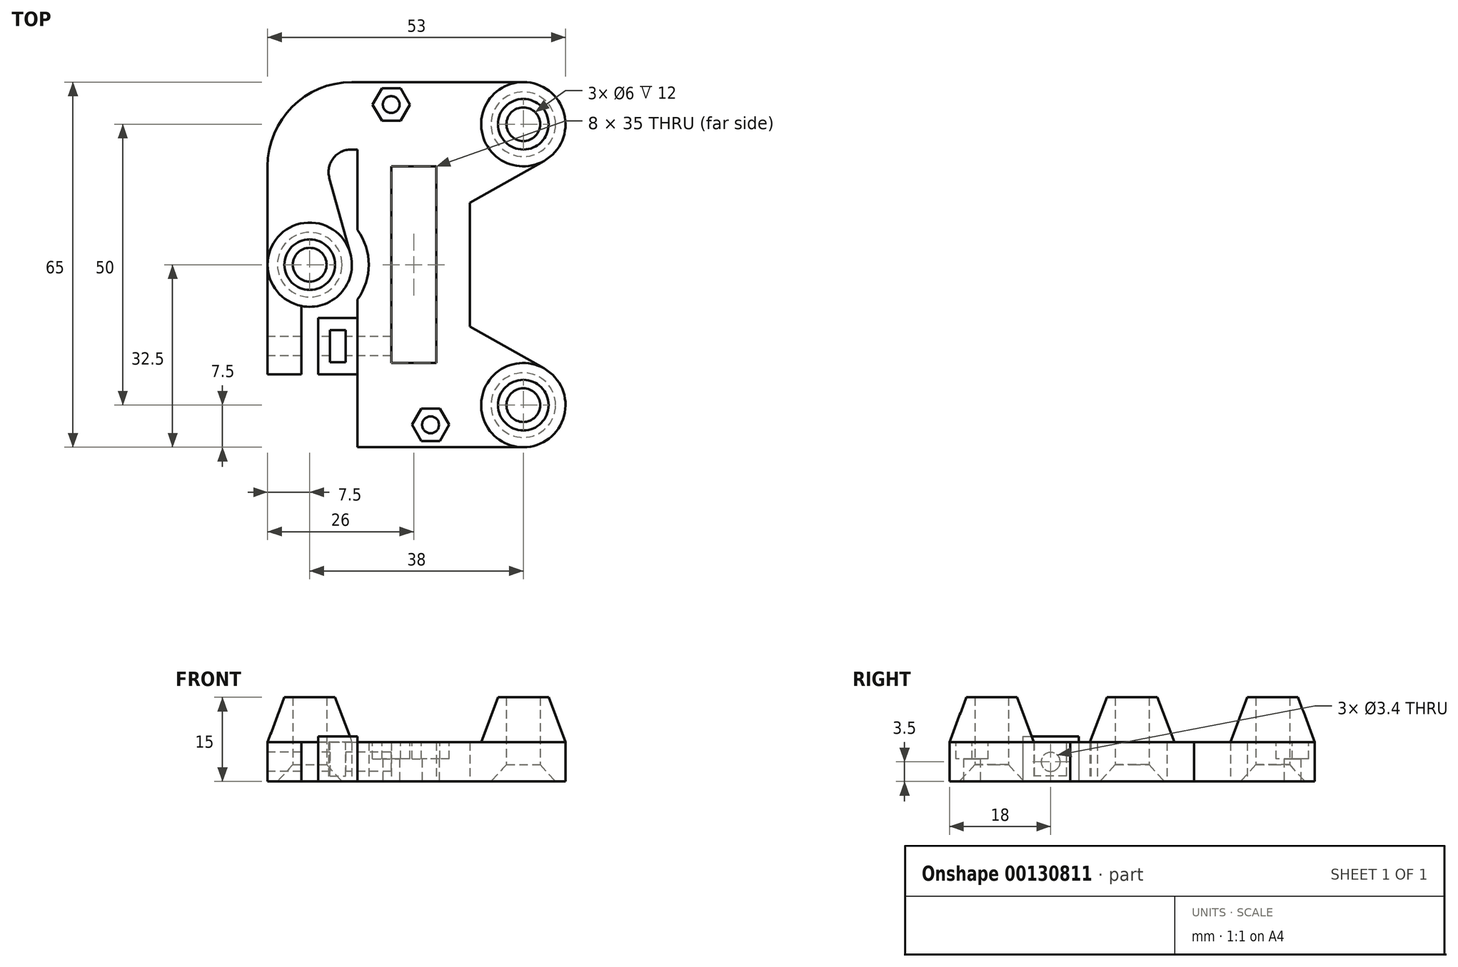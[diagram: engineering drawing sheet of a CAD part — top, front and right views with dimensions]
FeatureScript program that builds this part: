
annotation { "Feature Type Name" : "Feature", "Feature Type Description" : "" }
export const myFeature = defineFeature(function(context is Context, id is Id, definition is map)
    precondition{}
    {
        {
            var Q0;
            Q0=qCreatedBy(makeId("Top.planeOp"),FACE);
            var sketch = newSketch(context, id + "F0", { "sketchPlane" : qUnion([Q0])});
            skLineSegment(sketch, "E0.bottom", {"start": v(0, 0) * mm, "end": v(20, 0) * mm});
            skLineSegment(sketch, "E0.top", {"start": v(0, 65) * mm, "end": v(20, 65) * mm});
            skLineSegment(sketch, "E0.left", {"start": v(0, 0) * mm, "end": v(0, 26.34) * mm});
            skLineSegment(sketch, "E0.right", {"start": v(20, 0) * mm, "end": v(20, 65) * mm});
            skLineSegment(sketch, "E1.bottom", {"start": v(6, 50) * mm, "end": v(14, 50) * mm});
            skLineSegment(sketch, "E1.top", {"start": v(6, 15) * mm, "end": v(14, 15) * mm});
            skLineSegment(sketch, "E1.left", {"start": v(6, 50) * mm, "end": v(6, 15) * mm});
            skLineSegment(sketch, "E1.right", {"start": v(14, 50) * mm, "end": v(14, 15) * mm});
            skLineSegment(sketch, "E2.bottom", {"start": v(-7, 23) * mm, "end": v(0, 23) * mm});
            skLineSegment(sketch, "E2.top", {"start": v(-7, 13) * mm, "end": v(0, 13) * mm});
            skLineSegment(sketch, "E2.left", {"start": v(-7, 23) * mm, "end": v(-7, 13) * mm});
            skLineSegment(sketch, "E2.right", {"start": v(0, 23) * mm, "end": v(0, 13) * mm});
            skCircle(sketch, "E3", {"center": v(29.5, 7.5) * mm, "radius": 3 * mm});
            skCircle(sketch, "E4", {"center": v(29.5, 57.5) * mm, "radius": 3 * mm});
            skCircle(sketch, "E5", {"center": v(-8.5, 32.5) * mm, "radius": 7.5 * mm});
            skCircle(sketch, "E6", {"center": v(29.5, 57.5) * mm, "radius": 7.5 * mm});
            skCircle(sketch, "E7", {"center": v(29.5, 7.5) * mm, "radius": 7.5 * mm});
            skLineSegment(sketch, "E8", {"start": v(20, 0) * mm, "end": v(29.5, 0) * mm});
            skLineSegment(sketch, "E9", {"start": v(20, 65) * mm, "end": v(29.5, 65) * mm});
            skLineSegment(sketch, "E10", {"start": v(-1.27, 34.5) * mm, "end": v(-5, 47.93) * mm});
            skLineSegment(sketch, "E11", {"start": v(-16, 13) * mm, "end": v(-16, 50) * mm});
            skCircle(sketch, "E12", {"center": v(-8.5, 32.5) * mm, "radius": 3 * mm});
            skLineSegment(sketch, "E13", {"start": v(-16, 13) * mm, "end": v(-10, 13) * mm});
            skLineSegment(sketch, "E14", {"start": v(-10, 13) * mm, "end": v(-10, 25.15) * mm});
            skLineSegment(sketch, "E15", {"start": v(-1, 65) * mm, "end": v(0, 65) * mm});
            skCircle(sketch, "E16", {"center": v(6, 61) * mm, "radius": 1.5 * mm});
            skCircle(sketch, "E17", {"center": v(13, 4) * mm, "radius": 1.5 * mm});
            skLineSegment(sketch, "E18", {"start": v(33.2, 50.97) * mm, "end": v(20, 43.5) * mm});
            skLineSegment(sketch, "E19", {"start": v(33.2, 14.03) * mm, "end": v(20, 21.5) * mm});
            skPoint(sketch, "E20.visualSharp", {"position": v(-16, 65) * mm});
            skArc(sketch, "E20.filletArc", {"start": v(-1, 65) * mm, "mid": v(-11.6, 60.6) * mm, "end": v(-16, 50) * mm});
            skLineSegment(sketch, "E21", {"start": v(-1.15, 53) * mm, "end": v(0, 53) * mm});
            skPoint(sketch, "E22", {"position": v(20, 32.5) * mm});
            skArc(sketch, "E23", {"start": v(0, 26.34) * mm, "mid": v(2, 32.5) * mm, "end": v(0, 38.66) * mm});
            skLineSegment(sketch, "E24", {"start": v(6, 32.5) * mm, "end": v(2, 32.5) * mm});
            skLineSegment(sketch, "E25.trimOffspring", {"start": v(0, 38.66) * mm, "end": v(0, 65) * mm});
            skPoint(sketch, "E26.visualSharp", {"position": v(-6.4, 53) * mm});
            skArc(sketch, "E26.filletArc", {"start": v(-1.15, 53) * mm, "mid": v(-4.33, 51.42) * mm, "end": v(-5, 47.93) * mm});
            skPoint(sketch, "E27", {"position": v(37, 57.5) * mm});
            skSolve(sketch);
        }
        {
            var Q0;
            Q0=qSketchRegion(id+"F0",true);
            extrude(context, id + "F1", {"entities" : qUnion([Q0]), "depth" : 7 * mm});
        }
        {
            var Q0;
            Q0=makeQuery(id+"F1.opExtrude","CAP_FACE",FACE,{"disambiguationData":[OSD([sQuery(id+"F0.wireOp",EDGE,"E0.bottom"),sQuery(id+"F0.wireOp",EDGE,"E0.top"),sQuery(id+"F0.wireOp",EDGE,"E0.left"),sQuery(id+"F0.wireOp",EDGE,"E0.right"),sQuery(id+"F0.wireOp",EDGE,"E1.bottom"),sQuery(id+"F0.wireOp",EDGE,"E1.top"),sQuery(id+"F0.wireOp",EDGE,"E1.left"),sQuery(id+"F0.wireOp",EDGE,"E1.right"),sQuery(id+"F0.wireOp",EDGE,"E2.bottom"),sQuery(id+"F0.wireOp",EDGE,"E2.top"),sQuery(id+"F0.wireOp",EDGE,"E2.left"),sQuery(id+"F0.wireOp",EDGE,"E3"),sQuery(id+"F0.wireOp",EDGE,"E4"),sQuery(id+"F0.wireOp",EDGE,"E5"),sQuery(id+"F0.wireOp",EDGE,"E6"),sQuery(id+"F0.wireOp",EDGE,"E7"),sQuery(id+"F0.wireOp",EDGE,"E8"),sQuery(id+"F0.wireOp",EDGE,"E9"),sQuery(id+"F0.wireOp",EDGE,"E10"),sQuery(id+"F0.wireOp",EDGE,"E11"),sQuery(id+"F0.wireOp",EDGE,"E12"),sQuery(id+"F0.wireOp",EDGE,"E13"),sQuery(id+"F0.wireOp",EDGE,"E14"),sQuery(id+"F0.wireOp",EDGE,"E16"),sQuery(id+"F0.wireOp",EDGE,"E17"),sQuery(id+"F0.wireOp",EDGE,"E18"),sQuery(id+"F0.wireOp",EDGE,"E19"),sQuery(id+"F0.wireOp",EDGE,"E20.filletArc"),sQuery(id+"F0.wireOp",EDGE,"E23"),sQuery(id+"F0.wireOp",EDGE,"E25.trimOffspring"),sQuery(id+"F0.wireOp",EDGE,"E26.filletArc")])],"isStart":false});
            cPlane(context, id + "F2", {"entities" : qUnion([Q0]), "cplaneType" : CPlaneType.OFFSET, "offset" : 0 * mm, "width" : 150 * mm, "height" : 150 * mm});
        }
        {
            var Q0;
            Q0=qCreatedBy(id+"F2.planeOp",FACE);
            var sketch = newSketch(context, id + "F3", { "sketchPlane" : qUnion([Q0])});
            skCircle(sketch, "E28.cCircle", {"center": v(13, 4) * mm, "radius": 2.88 * mm, "construction": true});
            skLineSegment(sketch, "E28.0", {"start": v(14.66, 1.13) * mm, "end": v(11.34, 1.12) * mm});
            skLineSegment(sketch, "E28.1", {"start": v(11.34, 1.12) * mm, "end": v(9.68, 4) * mm});
            skLineSegment(sketch, "E28.2", {"start": v(9.68, 4) * mm, "end": v(11.34, 6.88) * mm});
            skLineSegment(sketch, "E28.3", {"start": v(11.34, 6.88) * mm, "end": v(14.66, 6.88) * mm});
            skLineSegment(sketch, "E28.4", {"start": v(14.66, 6.87) * mm, "end": v(16.32, 4) * mm});
            skLineSegment(sketch, "E28.5", {"start": v(16.32, 4) * mm, "end": v(14.66, 1.12) * mm});
            skPoint(sketch, "E28.0.midPoint", {"position": v(13, 1.13) * mm});
            skCircle(sketch, "E29.cCircle", {"center": v(6, 61) * mm, "radius": 2.88 * mm, "construction": true});
            skLineSegment(sketch, "E29.0", {"start": v(9.32, 61) * mm, "end": v(7.66, 58.13) * mm});
            skLineSegment(sketch, "E29.1", {"start": v(7.66, 58.12) * mm, "end": v(4.34, 58.12) * mm});
            skLineSegment(sketch, "E29.2", {"start": v(4.34, 58.12) * mm, "end": v(2.68, 61) * mm});
            skLineSegment(sketch, "E29.3", {"start": v(2.68, 61) * mm, "end": v(4.34, 63.87) * mm});
            skLineSegment(sketch, "E29.4", {"start": v(4.34, 63.88) * mm, "end": v(7.66, 63.88) * mm});
            skLineSegment(sketch, "E29.5", {"start": v(7.66, 63.88) * mm, "end": v(9.32, 61) * mm});
            skPoint(sketch, "E29.0.midPoint", {"position": v(8.49, 59.56) * mm});
            skSolve(sketch);
        }
        {
            var Q0;
            Q0=qSketchRegion(id+"F3",true);
            extrude(context, id + "F4", {"entities" : qUnion([Q0]), "operationType" : NewBodyOperationType.REMOVE, "flatOperationType" : FlatOperationType.REMOVE, "oppositeDirection" : true, "offsetDistance" : 25 * mm, "depth" : 3 * mm, "domain" : OperationDomain.MODEL});
        }
        {
            var Q0;
            Q0=qCreatedBy(id+"F2.planeOp",FACE);
            var sketch = newSketch(context, id + "F5", { "sketchPlane" : qUnion([Q0])});
            skLineSegment(sketch, "E30.bottom", {"start": v(-7, 13) * mm, "end": v(0, 13) * mm});
            skLineSegment(sketch, "E30.top", {"start": v(-7, 23) * mm, "end": v(0, 23) * mm});
            skLineSegment(sketch, "E30.left", {"start": v(-7, 13) * mm, "end": v(-7, 23) * mm});
            skLineSegment(sketch, "E30.right", {"start": v(0, 13) * mm, "end": v(0, 23) * mm});
            skSolve(sketch);
        }
        {
            var Q0;
            Q0=qSketchRegion(id+"F5",true);
            extrude(context, id + "F6", {"entities" : qUnion([Q0]), "operationType" : NewBodyOperationType.ADD, "depth" : 1 * mm});
        }
        {
            var Q0;
            Q0=makeQuery(id+"F6.opExtrude","CAP_FACE",FACE,{"disambiguationData":[OSD([sQuery(id+"F5.wireOp",EDGE,"E30.bottom"),sQuery(id+"F5.wireOp",EDGE,"E30.top"),sQuery(id+"F5.wireOp",EDGE,"E30.left"),sQuery(id+"F5.wireOp",EDGE,"E30.right")])],"isStart":false});
            cPlane(context, id + "F7", {"entities" : qUnion([Q0]), "cplaneType" : CPlaneType.OFFSET, "offset" : 0 * mm, "width" : 150 * mm, "height" : 150 * mm});
        }
        {
            var Q0;
            Q0=qCreatedBy(id+"F7.planeOp",FACE);
            var sketch = newSketch(context, id + "F8", { "sketchPlane" : qUnion([Q0])});
            skLineSegment(sketch, "E31.bottom", {"start": v(-4.87, 20.88) * mm, "end": v(-2.12, 20.88) * mm});
            skLineSegment(sketch, "E31.top", {"start": v(-4.87, 15.13) * mm, "end": v(-2.12, 15.13) * mm});
            skLineSegment(sketch, "E31.left", {"start": v(-4.87, 20.88) * mm, "end": v(-4.87, 15.12) * mm});
            skLineSegment(sketch, "E31.right", {"start": v(-2.12, 20.88) * mm, "end": v(-2.12, 15.12) * mm});
            skPoint(sketch, "E32", {"position": v(-2.12, 18) * mm});
            skPoint(sketch, "E33", {"position": v(-3.5, 20.88) * mm});
            skSolve(sketch);
        }
        {
            var Q0;
            Q0=makeQuery(id+"F8.imprint","IMPRINT",FACE,{"disambiguationData":[TD([[makeQuery(id+"F8.imprint","IMPRINT",EDGE,{"derivedFrom":sQuery(id+"F8.wireOp",EDGE,"E31.bottom")}),-1.0]])]});
            extrude(context, id + "F9", {"entities" : qUnion([Q0]), "operationType" : NewBodyOperationType.REMOVE, "oppositeDirection" : true, "depth" : 7 * mm});
        }
        {
            var Q0;
            Q0=makeQuery(id+"F1.opExtrude","SWEPT_FACE",FACE,{"disambiguationData":[OSD([sQuery(id+"F0.wireOp",EDGE,"E11")])]});
            cPlane(context, id + "F10", {"entities" : qUnion([Q0]), "cplaneType" : CPlaneType.OFFSET, "offset" : 0 * mm, "width" : 150 * mm, "height" : 150 * mm});
        }
        {
            var Q0;
            Q0=qCreatedBy(id+"F10.planeOp",FACE);
            var sketch = newSketch(context, id + "F11", { "sketchPlane" : qUnion([Q0])});
            skCircle(sketch, "E34", {"center": v(-18, 3.5) * mm, "radius": 1.7 * mm});
            skSolve(sketch);
        }
        {
            var Q0;
            Q0=qSketchRegion(id+"F11",true);
            var Q1;
            Q1=makeQuery(id+"F1.opExtrude","SWEPT_FACE",FACE,{"disambiguationData":[OSD([sQuery(id+"F0.wireOp",EDGE,"E1.right")])]});
            extrude(context, id + "F12", {"entities" : qUnion([Q0]), "operationType" : NewBodyOperationType.REMOVE, "endBound" : BoundingType.UP_TO_SURFACE, "oppositeDirection" : true, "endBoundEntityFace" : qUnion([Q1]), "depth" : 25 * mm});
        }
        {
            var Q0;
            Q0=makeQuery(id+"F1.opExtrude","SWEPT_FACE",FACE,{"disambiguationData":[OSD([sQuery(id+"F0.wireOp",EDGE,"E0.right")])]});
            var Q1;
            Q1=sQuery(id+"F0.wireOp",VERTEX,"E3.center");
            cPlane(context, id + "F13", {"entities" : qUnion([Q0, Q1]), "cplaneType" : CPlaneType.PLANE_POINT, "offset" : 8 * mm, "width" : 150 * mm, "height" : 150 * mm});
        }
        {
            var Q0;
            Q0=qCreatedBy(id+"F13.planeOp",FACE);
            var sketch = newSketch(context, id + "F14", { "sketchPlane" : qUnion([Q0])});
            skLineSegment(sketch, "E35", {"start": v(7.5, 15) * mm, "end": v(7.5, 0) * mm});
            skLineSegment(sketch, "E36", {"start": v(57.5, 15) * mm, "end": v(57.5, 0) * mm});
            skLineSegment(sketch, "E37", {"start": v(0, 7) * mm, "end": v(4.5, 7) * mm});
            skLineSegment(sketch, "E38", {"start": v(4.5, 7) * mm, "end": v(4.5, 15) * mm});
            skLineSegment(sketch, "E39", {"start": v(4.5, 15) * mm, "end": v(3, 15) * mm});
            skLineSegment(sketch, "E40", {"start": v(3, 15) * mm, "end": v(0, 7) * mm});
            skLineSegment(sketch, "E41", {"start": v(60.5, 7) * mm, "end": v(65, 7) * mm});
            skLineSegment(sketch, "E42", {"start": v(65, 7) * mm, "end": v(62, 15) * mm});
            skLineSegment(sketch, "E43", {"start": v(62, 15) * mm, "end": v(60.5, 15) * mm});
            skLineSegment(sketch, "E44", {"start": v(60.5, 15) * mm, "end": v(60.5, 7) * mm});
            skLineSegment(sketch, "E45", {"start": v(1.75, 0) * mm, "end": v(4.5, 3) * mm});
            skLineSegment(sketch, "E46", {"start": v(4.5, 3) * mm, "end": v(4.5, 0) * mm});
            skLineSegment(sketch, "E47", {"start": v(4.5, 0) * mm, "end": v(1.75, 0) * mm});
            skLineSegment(sketch, "E48", {"start": v(63.25, 0) * mm, "end": v(60.5, 3) * mm});
            skLineSegment(sketch, "E49", {"start": v(60.5, 3) * mm, "end": v(60.5, 0) * mm});
            skLineSegment(sketch, "E50", {"start": v(60.5, 0) * mm, "end": v(63.25, 0) * mm});
            skSolve(sketch);
        }
        {
            var Q0;
            Q0=makeQuery(id+"F14.imprint","IMPRINT",FACE,{"disambiguationData":[TD([[makeQuery(id+"F14.imprint","IMPRINT",EDGE,{"derivedFrom":sQuery(id+"F14.wireOp",EDGE,"E37")}),1.0]])]});
            var Q1;
            Q1=sQuery(id+"F14.wireOp",EDGE,"E35");
            revolve(context, id + "F15", {"operationType" : NewBodyOperationType.ADD, "entities" : qUnion([Q0]), "axis" : qUnion([Q1]), "revolveType" : RevolveType.FULL});
        }
        {
            var Q0;
            Q0=makeQuery(id+"F14.imprint","IMPRINT",FACE,{"disambiguationData":[TD([[makeQuery(id+"F14.imprint","IMPRINT",EDGE,{"derivedFrom":sQuery(id+"F14.wireOp",EDGE,"E41")}),1.0]])]});
            var Q1;
            Q1=sQuery(id+"F14.wireOp",EDGE,"E36");
            revolve(context, id + "F16", {"operationType" : NewBodyOperationType.ADD, "entities" : qUnion([Q0]), "axis" : qUnion([Q1]), "revolveType" : RevolveType.FULL});
        }
        {
            var Q0;
            Q0=makeQuery(id+"F14.imprint","IMPRINT",FACE,{"disambiguationData":[TD([[makeQuery(id+"F14.imprint","IMPRINT",EDGE,{"derivedFrom":sQuery(id+"F14.wireOp",EDGE,"E45")}),-1.0]])]});
            var Q1;
            Q1=sQuery(id+"F14.wireOp",EDGE,"E46");
            var Q2;
            Q2=sQuery(id+"F14.wireOp",EDGE,"E45");
            var Q3;
            Q3=sQuery(id+"F14.wireOp",EDGE,"E47");
            var Q4;
            Q4=sQuery(id+"F14.wireOp",EDGE,"E35");
            revolve(context, id + "F17", {"operationType" : NewBodyOperationType.REMOVE, "entities" : qUnion([Q0]), "surfaceEntities" : qUnion([Q1, Q2, Q3]), "axis" : qUnion([Q4]), "revolveType" : RevolveType.FULL, "oppositeDirection" : true});
        }
        {
            var Q0;
            Q0=makeQuery(id+"F14.imprint","IMPRINT",FACE,{"disambiguationData":[TD([[makeQuery(id+"F14.imprint","IMPRINT",EDGE,{"derivedFrom":sQuery(id+"F14.wireOp",EDGE,"E48")}),1.0]])]});
            var Q1;
            Q1=sQuery(id+"F14.wireOp",EDGE,"E36");
            revolve(context, id + "F18", {"operationType" : NewBodyOperationType.REMOVE, "entities" : qUnion([Q0]), "axis" : qUnion([Q1]), "revolveType" : RevolveType.FULL, "oppositeDirection" : true});
        }
        {
            var Q0;
            Q0=makeQuery(id+"F1.opExtrude","SWEPT_FACE",FACE,{"disambiguationData":[OSD([sQuery(id+"F0.wireOp",EDGE,"E11")])]});
            var Q1;
            Q1=sQuery(id+"F0.wireOp",VERTEX,"E12.center");
            cPlane(context, id + "F19", {"entities" : qUnion([Q0, Q1]), "cplaneType" : CPlaneType.PLANE_POINT, "offset" : 25 * mm, "width" : 150 * mm, "height" : 150 * mm});
        }
        {
            var Q0;
            Q0=qCreatedBy(id+"F19.planeOp",FACE);
            var sketch = newSketch(context, id + "F20", { "sketchPlane" : qUnion([Q0])});
            skLineSegment(sketch, "E51", {"start": v(-32.5, 15) * mm, "end": v(-32.5, 0) * mm});
            skLineSegment(sketch, "E52", {"start": v(-29.5, 0) * mm, "end": v(-29.5, 3) * mm});
            skLineSegment(sketch, "E53", {"start": v(-29.5, 3) * mm, "end": v(-26.75, 0) * mm});
            skLineSegment(sketch, "E54", {"start": v(-26.75, 0) * mm, "end": v(-29.5, 0) * mm});
            skLineSegment(sketch, "E55", {"start": v(-29.5, 7) * mm, "end": v(-29.5, 15) * mm});
            skLineSegment(sketch, "E56", {"start": v(-29.5, 15) * mm, "end": v(-28, 15) * mm});
            skLineSegment(sketch, "E57", {"start": v(-28, 15) * mm, "end": v(-25, 7) * mm});
            skLineSegment(sketch, "E58", {"start": v(-25, 7) * mm, "end": v(-29.5, 7) * mm});
            skSolve(sketch);
        }
        {
            var Q0;
            Q0=makeQuery(id+"F20.imprint","IMPRINT",FACE,{"disambiguationData":[TD([[makeQuery(id+"F20.imprint","IMPRINT",EDGE,{"derivedFrom":sQuery(id+"F20.wireOp",EDGE,"E55")}),-1.0]])]});
            var Q1;
            Q1=sQuery(id+"F20.wireOp",EDGE,"E51");
            revolve(context, id + "F21", {"operationType" : NewBodyOperationType.ADD, "entities" : qUnion([Q0]), "axis" : qUnion([Q1]), "revolveType" : RevolveType.FULL});
        }
        {
            var Q0;
            Q0=makeQuery(id+"F20.imprint","IMPRINT",FACE,{"disambiguationData":[TD([[makeQuery(id+"F20.imprint","IMPRINT",EDGE,{"derivedFrom":sQuery(id+"F20.wireOp",EDGE,"E52")}),-1.0]])]});
            var Q1;
            Q1=sQuery(id+"F20.wireOp",EDGE,"E51");
            revolve(context, id + "F22", {"operationType" : NewBodyOperationType.REMOVE, "entities" : qUnion([Q0]), "axis" : qUnion([Q1]), "revolveType" : RevolveType.FULL, "oppositeDirection" : true});
        }
    });
